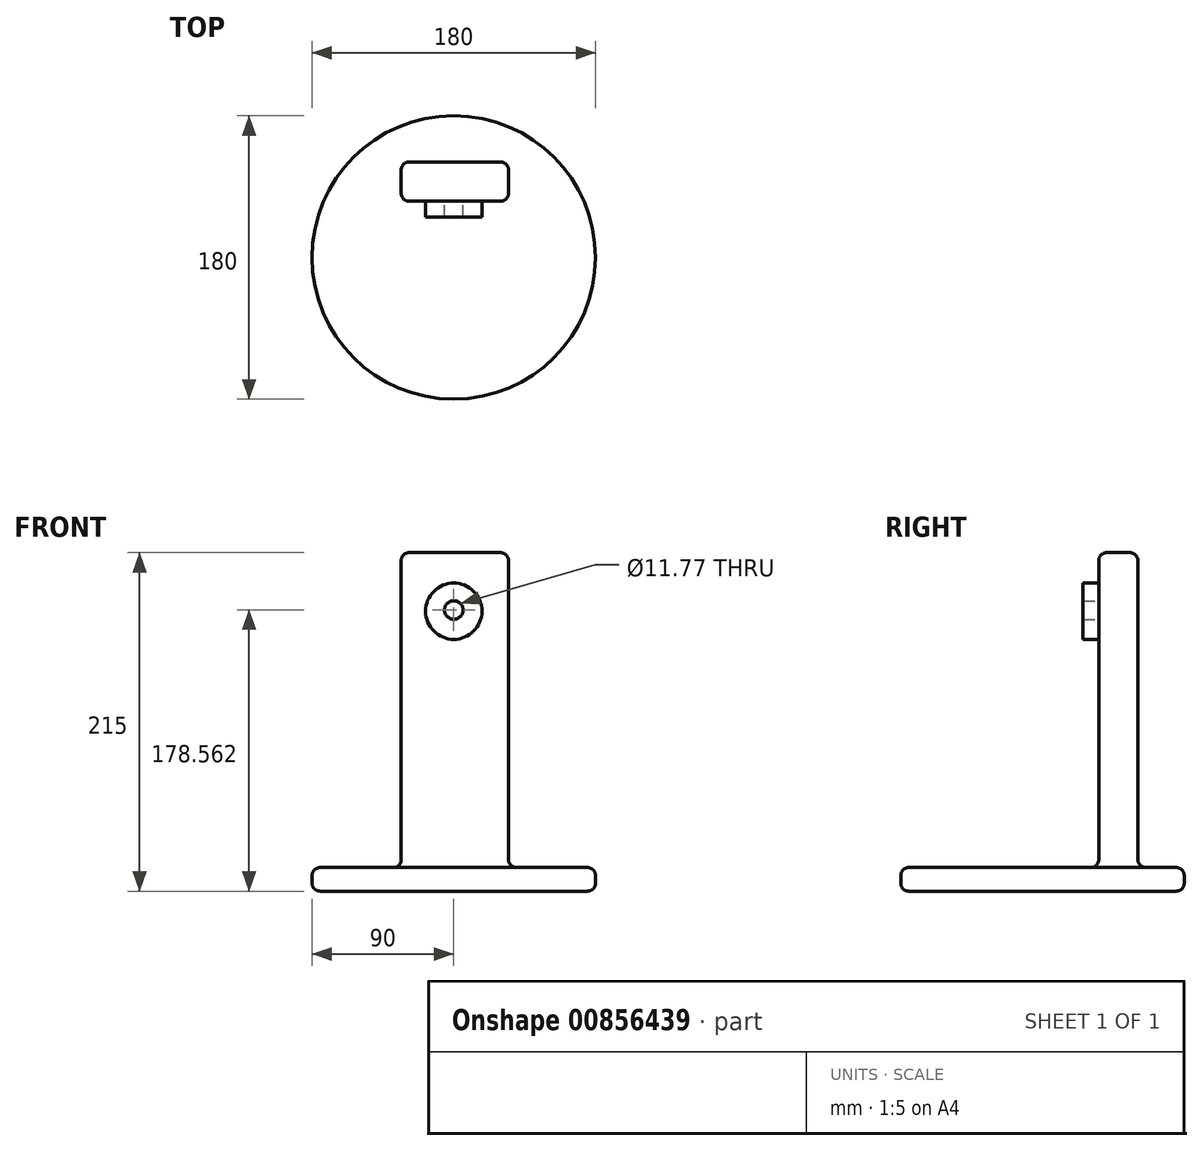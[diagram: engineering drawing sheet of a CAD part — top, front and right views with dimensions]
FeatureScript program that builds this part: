
annotation { "Feature Type Name" : "Feature", "Feature Type Description" : "" }
export const myFeature = defineFeature(function(context is Context, id is Id, definition is map)
    precondition{}
    {
        {
            var Q0;
            Q0=qCreatedBy(makeId("Top.planeOp"),FACE);
            var sketch = newSketch(context, id + "F0", { "sketchPlane" : qUnion([Q0])});
            skCircle(sketch, "E0", {"center": v(0, 0) * mm, "radius": 90 * mm});
            skSolve(sketch);
        }
        {
            var Q0;
            Q0=makeQuery(id+"F0.imprint","IMPRINT",FACE,{"disambiguationData":[TD([[makeQuery(id+"F0.imprint","IMPRINT",EDGE,{"derivedFrom":sQuery(id+"F0.wireOp",EDGE,"E0")}),1.0]])]});
            extrude(context, id + "F1", {"entities" : qUnion([Q0]), "depth" : 15 * mm, "offsetDistance" : 25 * mm});
        }
        {
            var Q0;
            Q0=makeQuery(id+"F1.opExtrude","CAP_FACE",FACE,{"disambiguationData":[OSD([sQuery(id+"F0.wireOp",EDGE,"E0")])],"isStart":false});
            var sketch = newSketch(context, id + "F2", { "sketchPlane" : qUnion([Q0])});
            skSolve(sketch);
        }
        {
            var Q0;
            Q0=makeQuery(id+"F2.imprint","IMPRINT",FACE,{"disambiguationData":[TD([[makeQuery(id+"F2.imprint","IMPRINT",EDGE,{"derivedFrom":makeQuery(id+"F1.opExtrude","CAP_EDGE",EDGE,{"disambiguationData":[OSD([sQuery(id+"F0.wireOp",EDGE,"E0")])],"isStart":false})}),1.0]])]});
            var sketch = newSketch(context, id + "F3", { "sketchPlane" : qUnion([Q0])});
            skLineSegment(sketch, "E1.bottom", {"start": v(-33.4, 60.63) * mm, "end": v(34.8, 60.63) * mm});
            skLineSegment(sketch, "E1.top", {"start": v(-33.4, 35.73) * mm, "end": v(34.8, 35.73) * mm});
            skLineSegment(sketch, "E1.left", {"start": v(-33.4, 60.63) * mm, "end": v(-33.4, 35.73) * mm});
            skLineSegment(sketch, "E1.right", {"start": v(34.8, 60.63) * mm, "end": v(34.8, 35.73) * mm});
            skSolve(sketch);
        }
        {
            var Q0;
            Q0=makeQuery(id+"F3.imprint","IMPRINT",FACE,{"disambiguationData":[TD([[makeQuery(id+"F3.imprint","IMPRINT",EDGE,{"derivedFrom":sQuery(id+"F3.wireOp",EDGE,"E1.bottom")}),-1.0]])]});
            extrude(context, id + "F4", {"entities" : qUnion([Q0]), "operationType" : NewBodyOperationType.ADD, "depth" : 200 * mm, "offsetDistance" : 25 * mm});
        }
        {
            var Q0;
            Q0=makeQuery(id+"F4.opExtrude","SWEPT_FACE",FACE,{"disambiguationData":[OSD([sQuery(id+"F3.wireOp",EDGE,"E1.top")])]});
            var sketch = newSketch(context, id + "F5", { "sketchPlane" : qUnion([Q0])});
            skCircle(sketch, "E2", {"center": v(0, 177.81) * mm, "radius": 17.91 * mm});
            skSolve(sketch);
        }
        {
            var Q0;
            Q0=makeQuery(id+"F5.imprint","IMPRINT",FACE,{"disambiguationData":[TD([[makeQuery(id+"F5.imprint","IMPRINT",EDGE,{"derivedFrom":sQuery(id+"F5.wireOp",EDGE,"E2")}),1.0]])]});
            var sketch = newSketch(context, id + "F6", { "sketchPlane" : qUnion([Q0])});
            skCircle(sketch, "E3", {"center": v(0, 178.56) * mm, "radius": 5.88 * mm});
            skSolve(sketch);
        }
        {
            var Q0;
            Q0=makeQuery(id+"F6.imprint","IMPRINT",FACE,{"disambiguationData":[TD([[makeQuery(id+"F6.imprint","IMPRINT",EDGE,{"derivedFrom":sQuery(id+"F6.wireOp",EDGE,"E3")}),-1.0]])]});
            extrude(context, id + "F7", {"entities" : qUnion([Q0]), "depth" : 10 * mm, "offsetDistance" : 25 * mm});
        }
        {
            var Q0;
            Q0=makeQuery(id+"F1.opExtrude","CAP_EDGE",EDGE,{"disambiguationData":[OSD([sQuery(id+"F0.wireOp",EDGE,"E0")])],"isStart":false});
            fillet(context, id + "F8", {"entities" : qUnion([Q0]), "radius" : 5 * mm, "tangentPropagation" : true, "allowEdgeOverflow" : false});
        }
        {
            var Q0;
            Q0=makeQuery(id+"F1.opExtrude","CAP_EDGE",EDGE,{"disambiguationData":[OSD([sQuery(id+"F0.wireOp",EDGE,"E0")])],"isStart":true});
            fillet(context, id + "F9", {"entities" : qUnion([Q0]), "radius" : 5 * mm, "tangentPropagation" : true, "allowEdgeOverflow" : false});
        }
        {
            var Q0;
            Q0=makeQuery(id+"F4.opExtrude","CAP_EDGE",EDGE,{"disambiguationData":[OSD([sQuery(id+"F3.wireOp",EDGE,"E1.top")])],"isStart":false});
            var Q1;
            Q1=makeQuery(id+"F4.opExtrude","SWEPT_EDGE",EDGE,{"disambiguationData":[OSD([sQuery(id+"F3.wireOp",EDGE,"E1.top"),sQuery(id+"F3.wireOp",EDGE,"E1.right")])]});
            fillet(context, id + "F10", {"entities" : qUnion([Q0, Q1]), "radius" : 5 * mm, "tangentPropagation" : true, "allowEdgeOverflow" : false});
        }
        {
            var Q0;
            Q0=makeQuery(id+"F4.opExtrude","SWEPT_EDGE",EDGE,{"disambiguationData":[OSD([sQuery(id+"F3.wireOp",EDGE,"E1.top"),sQuery(id+"F3.wireOp",EDGE,"E1.left")])]});
            var Q1;
            Q1=makeQuery(id+"F4.opExtrude","SWEPT_FACE",FACE,{"disambiguationData":[OSD([sQuery(id+"F3.wireOp",EDGE,"E1.left")])]});
            var Q2;
            Q2=makeQuery(id+"F4.opExtrude","SWEPT_FACE",FACE,{"disambiguationData":[OSD([sQuery(id+"F3.wireOp",EDGE,"E1.right")])]});
            var Q3;
            Q3=makeQuery(id+"F4.opExtrude","SWEPT_FACE",FACE,{"disambiguationData":[OSD([sQuery(id+"F3.wireOp",EDGE,"E1.bottom")])]});
            var Q4;
            Q4=makeQuery(id+"F4.opExtrude","CAP_FACE",FACE,{"disambiguationData":[OSD([sQuery(id+"F3.wireOp",EDGE,"E1.bottom"),sQuery(id+"F3.wireOp",EDGE,"E1.top"),sQuery(id+"F3.wireOp",EDGE,"E1.left"),sQuery(id+"F3.wireOp",EDGE,"E1.right")])],"isStart":false});
            fillet(context, id + "F11", {"entities" : qUnion([Q0, Q1, Q2, Q3, Q4]), "radius" : 5 * mm, "tangentPropagation" : true, "allowEdgeOverflow" : false});
        }
    });
